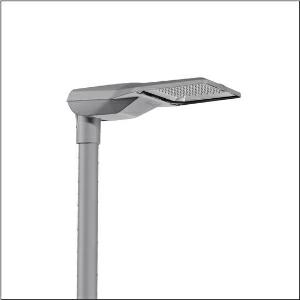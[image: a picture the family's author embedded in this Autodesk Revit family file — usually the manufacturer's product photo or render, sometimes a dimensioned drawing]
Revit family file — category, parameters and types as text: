
# Revit family: streetlight_sl_21_iq_midi___st0_8a_5xe3c21g08nb_deda
name_source: partatom
category: Lighting Fixtures
units: mm (PartAtom-declared; Revit-internal decimal feet)

## family parameters
Cut with Voids When Loaded = No
Host = Face
Light Source = No
Part Type = Normal
Room Calculation Point = No
Round Connector Dimension = Use Diameter
Shared = No

## types (1)
- --- (1 x LED, 19210 lm, 155.5 W, 2200K)
    Apparent Load = 155 VA
    CIE Flux Codes = 41 75 97 100 100
    Color Rendering = 70
    Color Temperature = 2200K
    Default Elevation = 1800 mm
    Description = Streetlight SL 21 iQ midi, mast luminaire, primary light control with lens, of PMMA, primary optical cover: cover, of toughened safety glass, transparent, light distribution: ST0.8a, light emission: direct distribution, primary light characteristic: asymmetric, installation type: post-top, side-entry, LED, High Power LED, rated luminous flux: 19.210lm, luminous efficacy: 124lm/W, light colour: 722, colour temperature: 2200K, control: Street-Remote, Auto-Match, Temp-Guard, Lumen-Switch, Night-Set, Smart-Wire, Light-Fading, Desk-Remote (wireless, voltage-free reading and setting of iQ features in the workshop via application-optimized NFC function/RFID function), optimised constant luminous flux control (CLO 2.0), presetting dimming linear, mains connection: 230..240V, AC, 50/60Hz, start of lifetime: 156W, end of service life: 162W, reduction: 69W, luminaire housing, of diecast aluminium, powder-coated, Siteco® metallic grey (DB 702S), corrosivity category C5 mid according to DIN EN ISO 12944, please order mast flange separately, inclination adjustable: 0°, 5°, 10°, 15°, sealing non-destructively replaceable, multi-level sealing system, length: 644mm, width: 335mm, height: 110mm, mast flange for spigot size: 42mm (side-entry): 5XC10008XM4, 60/48mm (side-entry/post-top): 5XC10108XM2, 76/60mm (side-entry/post-top): 5XC10108XM1, protection rating (complete): IP66, insulation class (complete): insulation class II (safety insulation), certification: CE, ENEC, ENEC+, VDE, impact resistance: IK09, permissible operating ambient temperature for outdoor applications: -40..+50°C, standard-compliant lighting for roads and squares, packaging unit: 1 piece

Light Distribution: ST0.8a
    Height = 111 mm
    Lamp = 1 x LED
    Lamp Light Flux = 19210 lm
    Lamp Power = 155.5 W
    Lamp count = 1
    Length = 644 mm
    Luminous efficacy = 124 lm/W
    Manufacturer = Siteco
    ModVariant = No
    Model = 5XE3C21G08NB
    Number of Poles = 1
    OnlyDefault = Yes
    Power Factor = 1
    Product Name = Streetlight SL 21 iQ midi | ST0.8a
    Product group = mast luminaire | pylon top
    ProductGroupID = 6100
    Protection Class = Protection class II
    Protection Degree = IP 66
    RLX_Detail_Level = 1
    RLX_Emergency_Light_Flux = 0 lm
    RLX_Emergency_Type = 0
    RLX_Emergency_Type_DB = No
    RlxData = <blob elided: 91245 chars, md5=957665c5>
    Socket = socket
    Standby Power = 0 W
    System Light Flux = 19210 lm
    System Power = 155 W
    Type Comments = factory setting: luminous flux: 100 % | dim-lin: 254 | 823 mA
    Type Image = l_1004298.jpg
    URL = http://relux.com
    VarID = @adj_101465
    Voltage = 0 V
    Weight = 0.00 kg
    Width = 336 mm

## geometry (parser evidence)
native form markers: Blend x4, Sweep x11
no freeform markers — native parametric forms only
